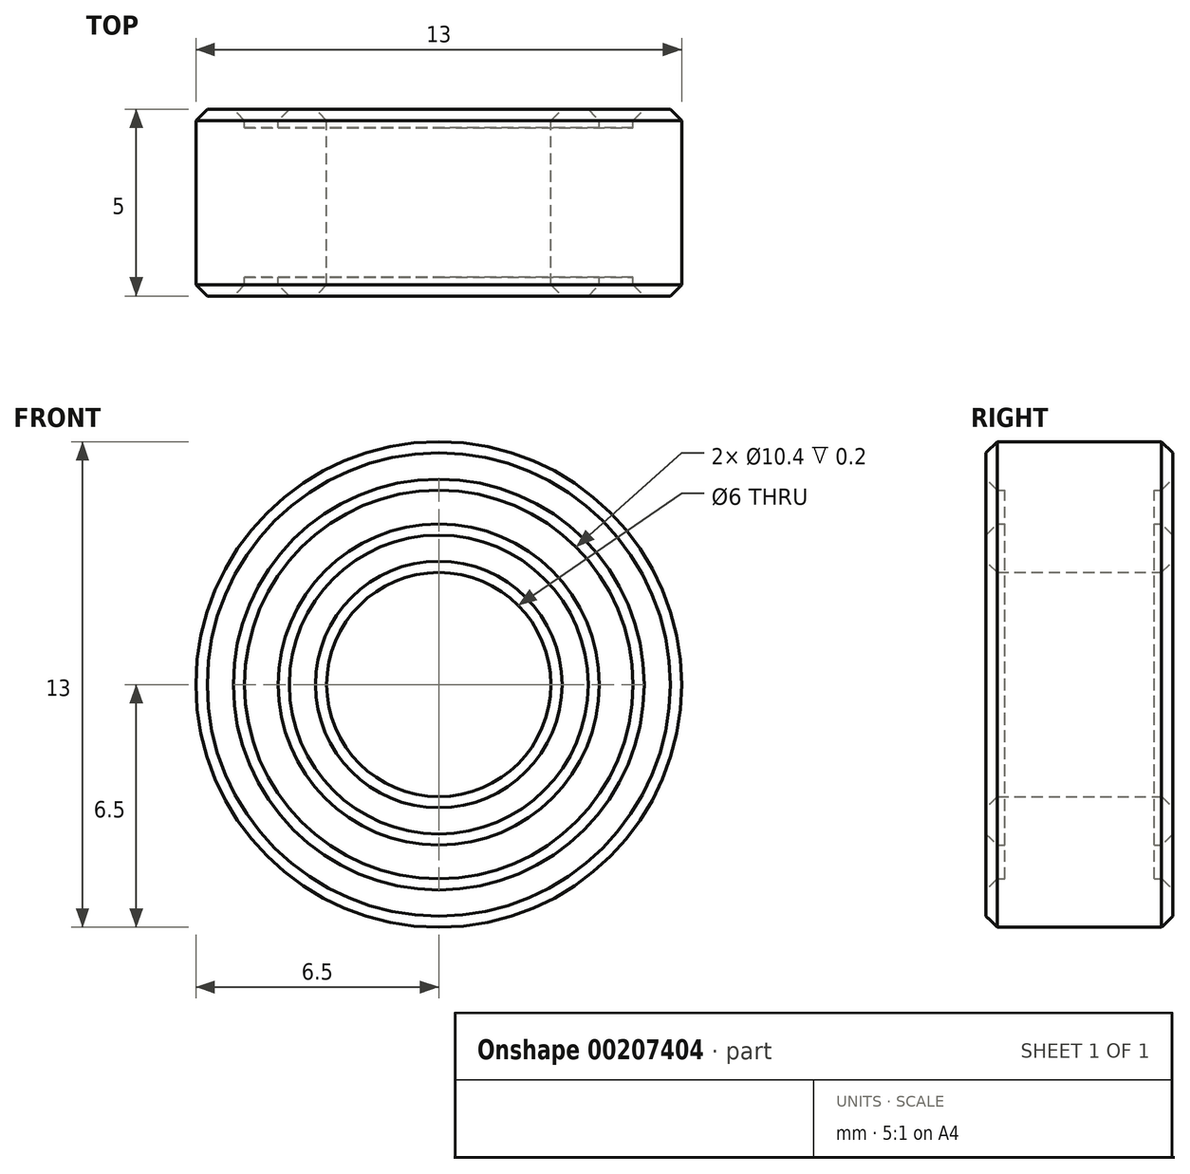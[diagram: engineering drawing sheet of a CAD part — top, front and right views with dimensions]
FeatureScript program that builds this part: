
annotation { "Feature Type Name" : "Feature", "Feature Type Description" : "" }
export const myFeature = defineFeature(function(context is Context, id is Id, definition is map)
    precondition{}
    {
        {
            assignVariable(context, id + "F0", {"name" : "depth", "anyValue" : 5});
        }
        {
            var Q0;
            Q0=qCreatedBy(makeId("Front.planeOp"),FACE);
            var sketch = newSketch(context, id + "F1", { "sketchPlane" : qUnion([Q0])});
            skCircle(sketch, "E0", {"center": v(0, 0) * mm, "radius": 6.5 * mm});
            skCircle(sketch, "E1", {"center": v(0, 0) * mm, "radius": 5.2 * mm});
            skCircle(sketch, "E2", {"center": v(0, 0) * mm, "radius": 4.3 * mm});
            skCircle(sketch, "E3", {"center": v(0, 0) * mm, "radius": 3 * mm});
            skSolve(sketch);
        }
        {
            var Q0;
            Q0=makeQuery(id+"F1.imprint","IMPRINT",FACE,{"disambiguationData":[TD([[makeQuery(id+"F1.imprint","IMPRINT",EDGE,{"derivedFrom":sQuery(id+"F1.wireOp",EDGE,"E0")}),1.0]])]});
            var Q1;
            Q1=makeQuery(id+"F1.imprint","IMPRINT",FACE,{"disambiguationData":[TD([[makeQuery(id+"F1.imprint","IMPRINT",EDGE,{"derivedFrom":sQuery(id+"F1.wireOp",EDGE,"E2")}),1.0]])]});
            extrude(context, id + "F2", {"entities" : qUnion([Q0, Q1]), "offsetDistance" : 25 * mm, "depth" : (getVariable(context, 'depth')) * mm, "symmetric" : true});
        }
        {
            var Q0;
            Q0=makeQuery(id+"F1.imprint","IMPRINT",FACE,{"disambiguationData":[TD([[makeQuery(id+"F1.imprint","IMPRINT",EDGE,{"derivedFrom":sQuery(id+"F1.wireOp",EDGE,"E1")}),1.0]])]});
            extrude(context, id + "F3", {"entities" : qUnion([Q0]), "operationType" : NewBodyOperationType.ADD, "offsetDistance" : 25 * mm, "depth" : (getVariable(context, 'depth') - 1) * mm, "symmetric" : true});
        }
        {
            var Q0;
            Q0=makeQuery(id+"F2.opExtrude","CAP_FACE",FACE,{"disambiguationData":[OSD([sQuery(id+"F1.wireOp",EDGE,"E0"),sQuery(id+"F1.wireOp",EDGE,"E1")])],"isStart":false});
            var Q1;
            Q1=makeQuery(id+"F2.opExtrude","CAP_FACE",FACE,{"disambiguationData":[OSD([sQuery(id+"F1.wireOp",EDGE,"E2"),sQuery(id+"F1.wireOp",EDGE,"E3")])],"isStart":false});
            var Q2;
            Q2=makeQuery(id+"F2.opExtrude","CAP_FACE",FACE,{"disambiguationData":[OSD([sQuery(id+"F1.wireOp",EDGE,"E0"),sQuery(id+"F1.wireOp",EDGE,"E1")])],"isStart":true});
            var Q3;
            Q3=makeQuery(id+"F2.opExtrude","CAP_FACE",FACE,{"disambiguationData":[OSD([sQuery(id+"F1.wireOp",EDGE,"E2"),sQuery(id+"F1.wireOp",EDGE,"E3")])],"isStart":true});
            chamfer(context, id + "F4", {"entities" : qUnion([Q0, Q1, Q2, Q3]), "width" : .3 * mm, "tangentPropagation" : true});
        }
    });
